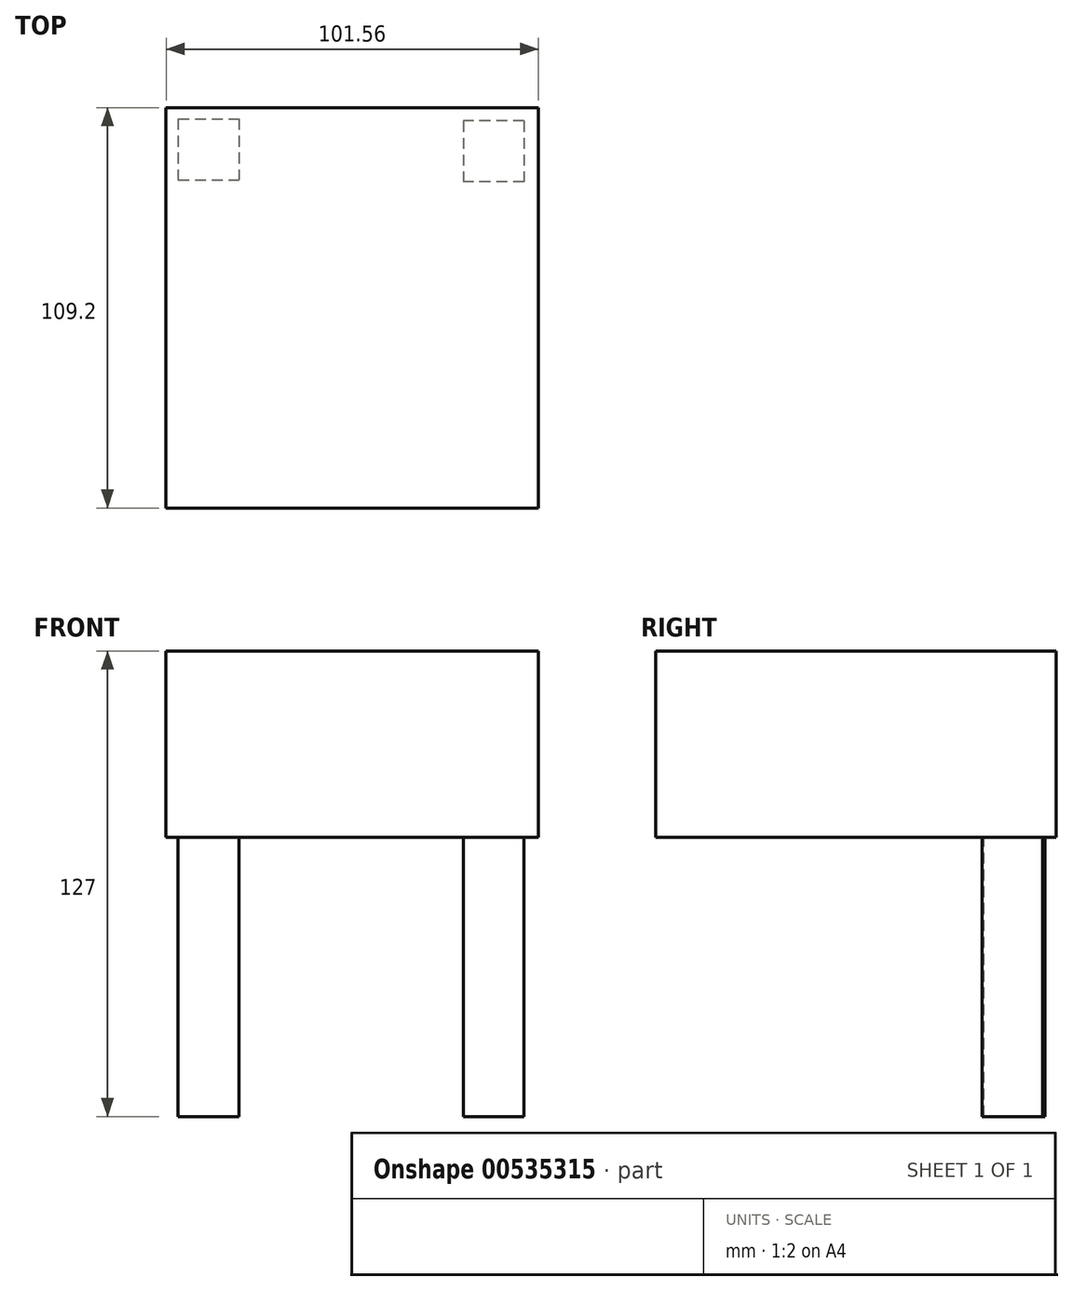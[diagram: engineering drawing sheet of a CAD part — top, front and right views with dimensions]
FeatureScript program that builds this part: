
annotation { "Feature Type Name" : "Feature", "Feature Type Description" : "" }
export const myFeature = defineFeature(function(context is Context, id is Id, definition is map)
    precondition{}
    {
        {
            var Q0;
            Q0=qCreatedBy(makeId("Top.planeOp"),FACE);
            var sketch = newSketch(context, id + "F0", { "sketchPlane" : qUnion([Q0])});
            skLineSegment(sketch, "E0.bottom", {"start": v(-50.78, 54.6) * mm, "end": v(50.78, 54.6) * mm});
            skLineSegment(sketch, "E0.top", {"start": v(-50.78, -54.6) * mm, "end": v(50.78, -54.6) * mm});
            skLineSegment(sketch, "E0.left", {"start": v(-50.78, 54.6) * mm, "end": v(-50.78, -54.6) * mm});
            skLineSegment(sketch, "E0.right", {"start": v(50.78, 54.6) * mm, "end": v(50.78, -54.6) * mm});
            skPoint(sketch, "E0.middle", {"position": v(0, 0) * mm});
            skSolve(sketch);
        }
        {
            var Q0;
            Q0=makeQuery(id+"F0.imprint","IMPRINT",FACE,{"disambiguationData":[TD([[makeQuery(id+"F0.imprint","IMPRINT",EDGE,{"derivedFrom":sQuery(id+"F0.wireOp",EDGE,"E0.bottom")}),-1.0]])]});
            extrude(context, id + "F1", {"entities" : qUnion([Q0]), "depth" : 50.8 * mm, "offsetDistance" : 25.4 * mm});
        }
        {
            var Q0;
            Q0=qCreatedBy(makeId("Top.planeOp"),FACE);
            var sketch = newSketch(context, id + "F2", { "sketchPlane" : qUnion([Q0])});
            skLineSegment(sketch, "E1.bottom", {"start": v(-47.5, 51.53) * mm, "end": v(-30.91, 51.53) * mm});
            skLineSegment(sketch, "E1.top", {"start": v(-47.5, 34.94) * mm, "end": v(-30.91, 34.94) * mm});
            skLineSegment(sketch, "E1.left", {"start": v(-47.5, 51.53) * mm, "end": v(-47.5, 34.94) * mm});
            skLineSegment(sketch, "E1.right", {"start": v(-30.91, 51.53) * mm, "end": v(-30.91, 34.94) * mm});
            skSolve(sketch);
        }
        {
            var Q0;
            Q0 = qSketchRegion(id + "F2", true);
            extrude(context, id + "F3", {"entities" : qUnion([Q0]), "operationType" : NewBodyOperationType.ADD, "oppositeDirection" : true, "depth" : 76.2 * mm, "offsetDistance" : 25.4 * mm});
        }
        {
            var Q0;
            Q0=qCreatedBy(makeId("Top.planeOp"),FACE);
            var sketch = newSketch(context, id + "F4", { "sketchPlane" : qUnion([Q0])});
            skLineSegment(sketch, "E2.bottom", {"start": v(46.88, 50.96) * mm, "end": v(30.34, 50.96) * mm});
            skLineSegment(sketch, "E2.top", {"start": v(46.88, 34.42) * mm, "end": v(30.34, 34.42) * mm});
            skLineSegment(sketch, "E2.left", {"start": v(46.88, 50.96) * mm, "end": v(46.88, 34.42) * mm});
            skLineSegment(sketch, "E2.right", {"start": v(30.34, 50.96) * mm, "end": v(30.34, 34.42) * mm});
            skLineSegment(sketch, "E3.bottom", {"start": v(30.34, 50.96) * mm, "end": v(46.88, 50.96) * mm});
            skLineSegment(sketch, "E3.top", {"start": v(30.34, 34.42) * mm, "end": v(46.88, 34.42) * mm});
            skSolve(sketch);
        }
        {
            var Q0;
            Q0 = qSketchRegion(id + "F4", true);
            extrude(context, id + "F5", {"entities" : qUnion([Q0]), "operationType" : NewBodyOperationType.ADD, "oppositeDirection" : true, "depth" : 76.2 * mm, "offsetDistance" : 25.4 * mm});
        }
    });
